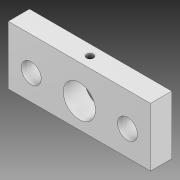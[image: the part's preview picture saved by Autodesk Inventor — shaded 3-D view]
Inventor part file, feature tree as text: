
AUTODESK INVENTOR PART (.ipt)
format: ipt  version: 2020 (Build 240168000, 168)  size: 123,392 bytes
history: native  units: mm
features: extrude x2, sketch x2
ambient origin geometry x8: Origin, YZ Plane, XZ Plane, XY Plane, X Axis, Y Axis, Z Axis, Center Point
bodies: Solid1 (feature_tree)
feature tree (4):
  extrude  "Extrusion1"  Depth=23.81mm
  extrude  "Extrusion2"  Depth=57.5mm
  sketch  "Sketch1"  dims[d0=38.5mm d1=23.81mm]
  sketch  "Sketch2"  dims[d2=23.81mm d3=57.5mm d4=57.5mm d5=170.0mm d6=85.0mm d7=70.0mm d8=40.0mm d9=25.4mm d10=0.0mm d11=8.43mm d12=12.7mm d13=85.0mm d14=25.4mm d15=0.0mm]
